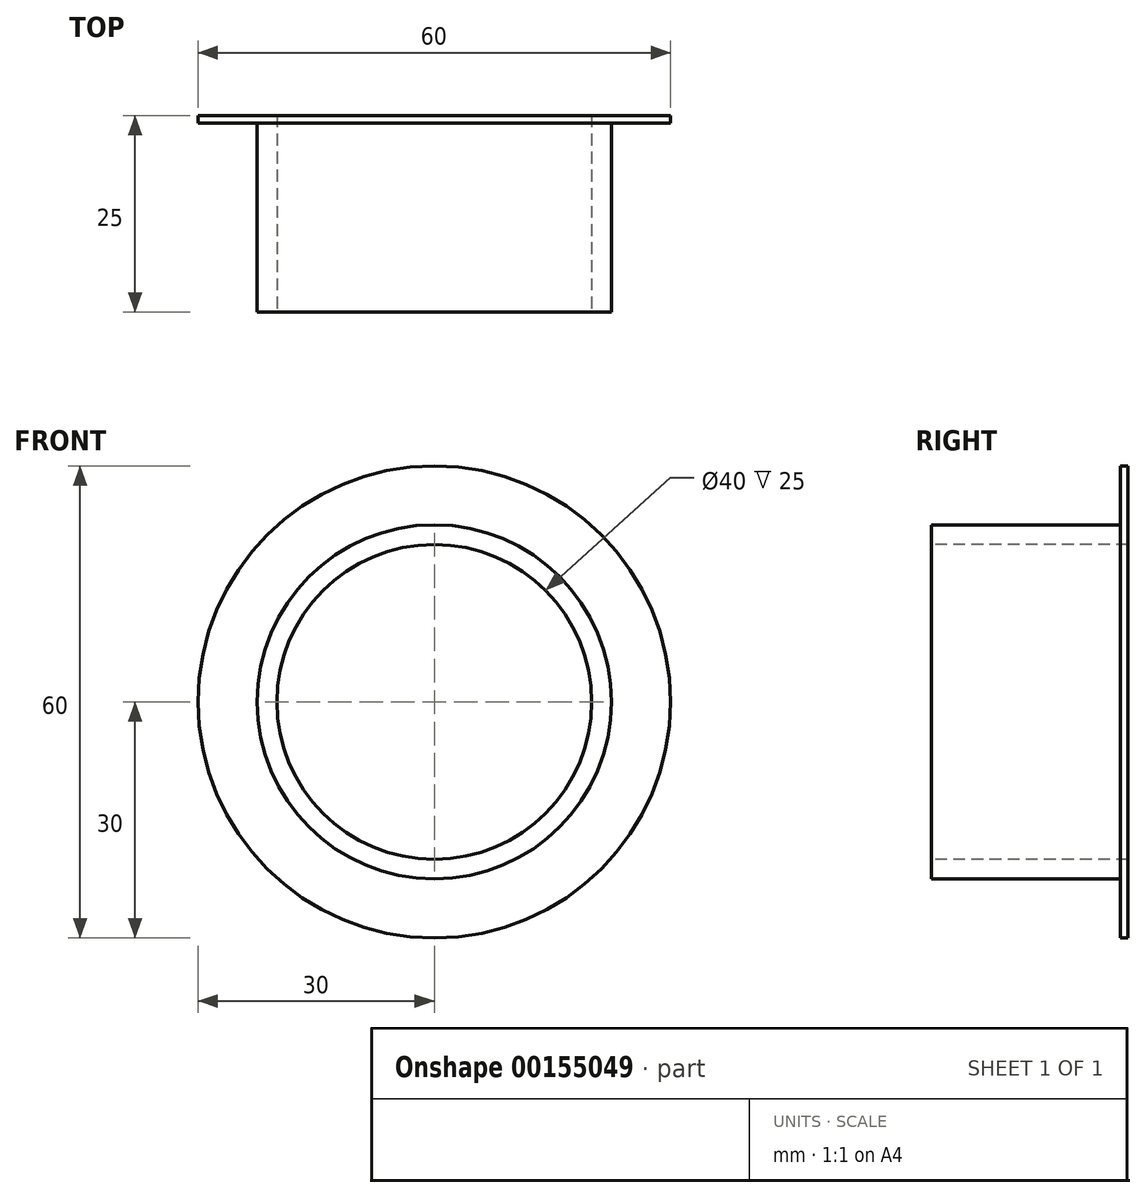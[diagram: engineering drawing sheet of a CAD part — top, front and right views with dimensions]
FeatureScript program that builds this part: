
annotation { "Feature Type Name" : "Feature", "Feature Type Description" : "" }
export const myFeature = defineFeature(function(context is Context, id is Id, definition is map)
    precondition{}
    {
        {
            var Q0;
            Q0=qCreatedBy(makeId("Front.planeOp"),FACE);
            var sketch = newSketch(context, id + "F0", { "sketchPlane" : qUnion([Q0])});
            skCircle(sketch, "E0", {"center": v(0, 0) * mm, "radius": 30 * mm});
            skSolve(sketch);
        }
        {
            var Q0;
            Q0=makeQuery(id+"F0.imprint","IMPRINT",FACE,{"disambiguationData":[TD([[makeQuery(id+"F0.imprint","IMPRINT",EDGE,{"derivedFrom":sQuery(id+"F0.wireOp",EDGE,"E0")}),1.0]])]});
            extrude(context, id + "F1", {"entities" : qUnion([Q0]), "depth" : 1 * mm});
        }
        {
            var Q0;
            Q0=makeQuery(id+"F1.opExtrude","CAP_FACE",FACE,{"disambiguationData":[OSD([sQuery(id+"F0.wireOp",EDGE,"E0")])],"isStart":false});
            var sketch = newSketch(context, id + "F2", { "sketchPlane" : qUnion([Q0])});
            skCircle(sketch, "E1", {"center": v(0, 0) * mm, "radius": 22.5 * mm});
            skSolve(sketch);
        }
        {
            var Q0;
            Q0=makeQuery(id+"F2.imprint","IMPRINT",FACE,{"disambiguationData":[TD([[makeQuery(id+"F2.imprint","IMPRINT",EDGE,{"derivedFrom":sQuery(id+"F2.wireOp",EDGE,"E1")}),1.0]])]});
            extrude(context, id + "F3", {"entities" : qUnion([Q0]), "operationType" : NewBodyOperationType.ADD, "depth" : 24 * mm});
        }
        {
            var Q0;
            Q0=makeQuery(id+"F1.opExtrude","SWEPT_FACE",FACE,{"disambiguationData":[OSD([sQuery(id+"F0.wireOp",EDGE,"E0")])]});
            var Q1;
            Q1=makeQuery(id+"F3.opExtrude","CAP_FACE",FACE,{"disambiguationData":[OSD([sQuery(id+"F2.wireOp",EDGE,"E1")])],"isStart":false});
            var Q2;
            Q2=makeQuery(id+"F3.opExtrude","CAP_EDGE",EDGE,{"disambiguationData":[OSD([sQuery(id+"F2.wireOp",EDGE,"E1")])],"isStart":false});
            var Q3;
            Q3=makeQuery(id+"F1.opExtrude","CAP_EDGE",EDGE,{"disambiguationData":[OSD([sQuery(id+"F0.wireOp",EDGE,"E0")])],"isStart":false});
            loft(context, id + "F4", {"bodyType" : ToolBodyType.SURFACE, "sheetProfilesArray" : [{ "sheetProfileEntities" : qUnion([Q0]) }, { "sheetProfileEntities" : qUnion([Q1]) }], "wireProfilesArray" : [{ "wireProfileEntities" : qUnion([Q2]) }, { "wireProfileEntities" : qUnion([Q3]) }]});
        }
        {
            var Q0;
            Q0=makeQuery(id+"F3.opExtrude","CAP_FACE",FACE,{"disambiguationData":[OSD([sQuery(id+"F2.wireOp",EDGE,"E1")])],"isStart":false});
            var sketch = newSketch(context, id + "F5", { "sketchPlane" : qUnion([Q0])});
            skCircle(sketch, "E2", {"center": v(0, 0) * mm, "radius": 20 * mm});
            skSolve(sketch);
        }
        {
            var Q0;
            Q0=makeQuery(id+"F5.imprint","IMPRINT",FACE,{"disambiguationData":[TD([[makeQuery(id+"F5.imprint","IMPRINT",EDGE,{"derivedFrom":sQuery(id+"F5.wireOp",EDGE,"E2")}),1.0]])]});
            extrude(context, id + "F6", {"entities" : qUnion([Q0]), "operationType" : NewBodyOperationType.REMOVE, "endBound" : BoundingType.THROUGH_ALL, "oppositeDirection" : true, "depth" : 25 * mm});
        }
    });
